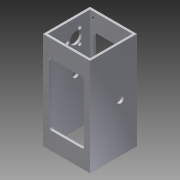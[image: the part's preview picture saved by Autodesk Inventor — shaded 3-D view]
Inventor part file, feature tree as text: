
AUTODESK INVENTOR PART (.ipt)
format: ipt  version: 2015 (Build 190159000, 159)  size: 188,416 bytes
history: native  units: mm
features: sketch x6, hole x4, thread x4, extrude x2, other x1, fillet x1, pattern_circular x1
ambient origin geometry x8: Origin, YZ Plane, XZ Plane, XY Plane, X Axis, Y Axis, Z Axis, Center Point
bodies: Body1 (feature_tree)
feature tree (19):
  other  "ソリッド1"
  extrude  "押し出し1"  Depth=40.0mm
  extrude  "押し出し2"  Depth=40.0mm
  fillet  "フィレット1"  Radius=2.0mm
  hole  "穴1"  [1 undecoded]
  thread  "ねじ1"
  thread  "ねじ2"
  thread  "ねじ3"
  thread  "ねじ4"
  hole  "穴3"  [1 undecoded]
  hole  "穴4"  [1 undecoded]
  pattern_circular  "円形状パターン1"  [2 undecoded]
  hole  "穴5"  [1 undecoded]
  sketch  "スケッチ1"
  sketch  "スケッチ3"
  sketch  "スケッチ4"
  sketch  "スケッチ6"
  sketch  "スケッチ7"
  sketch  "スケッチ8"
note: 6 required parameter values undecoded (feature->parameter linkage not recoverable at this tier; creation-order binding heuristic only, values carry confidence <= 0.55)
